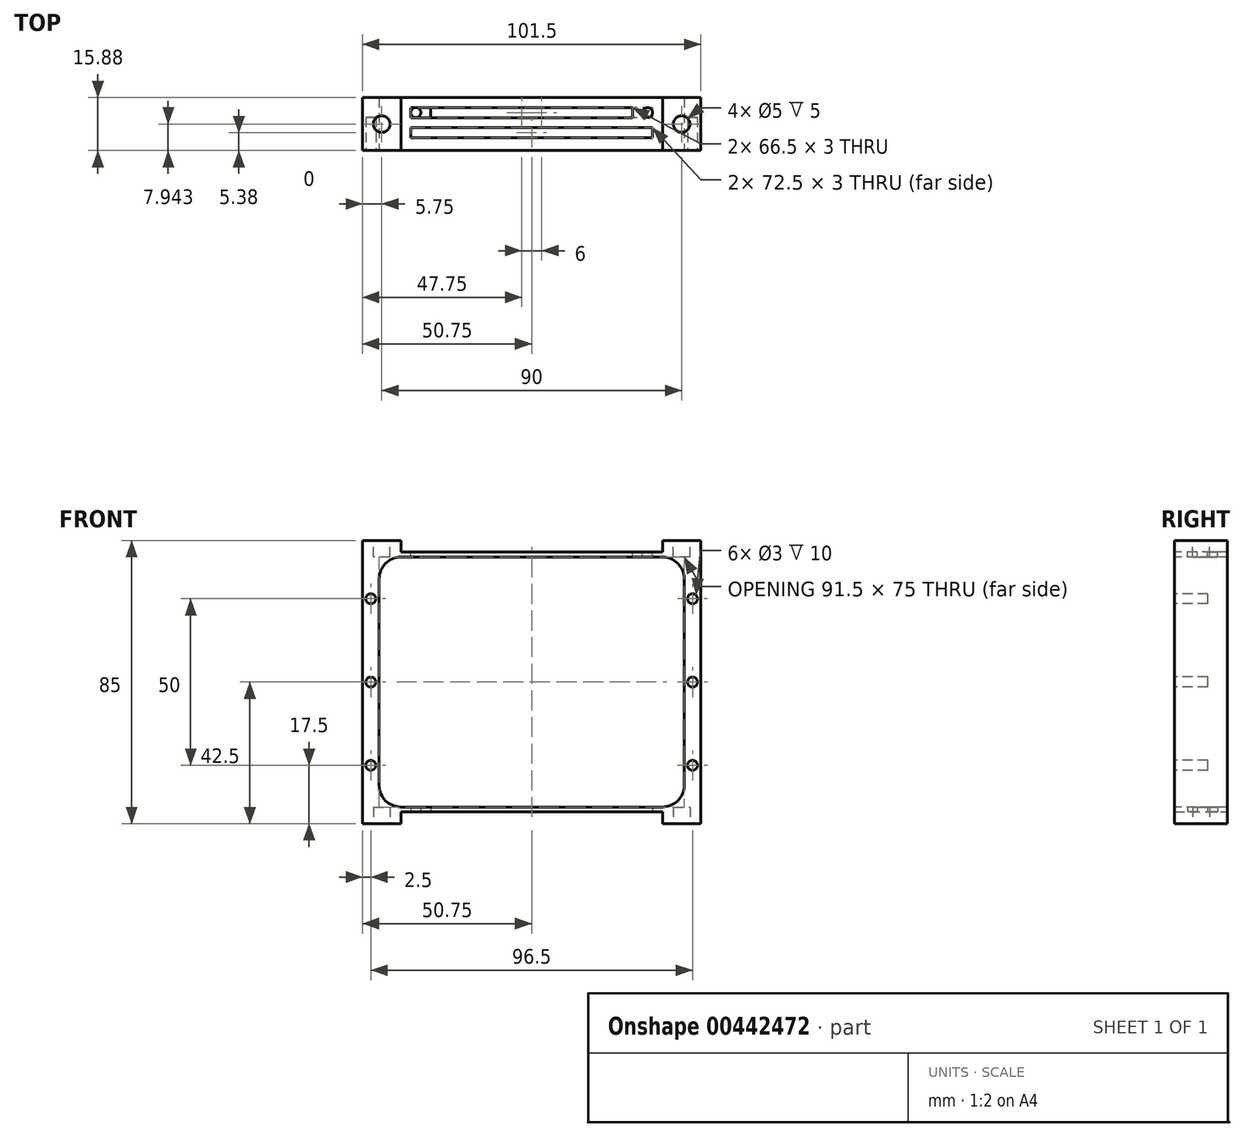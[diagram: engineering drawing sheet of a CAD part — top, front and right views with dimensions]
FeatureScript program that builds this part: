
annotation { "Feature Type Name" : "Feature", "Feature Type Description" : "" }
export const myFeature = defineFeature(function(context is Context, id is Id, definition is map)
    precondition{}
    {
        {
            var Q0;
            Q0=qCreatedBy(makeId("Front.planeOp"),FACE);
            var sketch = newSketch(context, id + "F0", { "sketchPlane" : qUnion([Q0])});
            skLineSegment(sketch, "E0.bottom", {"start": v(50.75, 42.5) * mm, "end": v(-50.75, 42.5) * mm});
            skLineSegment(sketch, "E0.top", {"start": v(50.75, -42.5) * mm, "end": v(-50.75, -42.5) * mm});
            skLineSegment(sketch, "E0.left", {"start": v(50.75, 42.5) * mm, "end": v(50.75, -42.5) * mm});
            skLineSegment(sketch, "E0.right", {"start": v(-50.75, 42.5) * mm, "end": v(-50.75, -42.5) * mm});
            skPoint(sketch, "E0.middle", {"position": v(0, 0) * mm});
            skSolve(sketch);
        }
        {
            var Q0;
            Q0=qSketchRegion(id+"F0",true);
            extrude(context, id + "F1", {"entities" : qUnion([Q0]), "depth" : 15.88 * mm});
        }
        {
            var Q0;
            Q0=makeQuery(id+"F1.opExtrude","CAP_FACE",FACE,{"disambiguationData":[OSD([sQuery(id+"F0.wireOp",EDGE,"E0.bottom"),sQuery(id+"F0.wireOp",EDGE,"E0.top"),sQuery(id+"F0.wireOp",EDGE,"E0.left"),sQuery(id+"F0.wireOp",EDGE,"E0.right")])],"isStart":false});
            var sketch = newSketch(context, id + "F2", { "sketchPlane" : qUnion([Q0])});
            skLineSegment(sketch, "E1.bottom", {"start": v(45.75, 37.5) * mm, "end": v(-45.75, 37.5) * mm, "construction": true});
            skLineSegment(sketch, "E1.top", {"start": v(45.75, -37.5) * mm, "end": v(-45.75, -37.5) * mm, "construction": true});
            skLineSegment(sketch, "E1.left", {"start": v(45.75, 37.5) * mm, "end": v(45.75, -37.5) * mm, "construction": true});
            skLineSegment(sketch, "E1.right", {"start": v(-45.75, 37.5) * mm, "end": v(-45.75, -37.5) * mm, "construction": true});
            skPoint(sketch, "E1.middle", {"position": v(0, 0) * mm});
            skCircle(sketch, "E2", {"center": v(-39.25, -31) * mm, "radius": 6.5 * mm, "construction": true});
            skCircle(sketch, "E3", {"center": v(39.25, -31) * mm, "radius": 6.5 * mm, "construction": true});
            skCircle(sketch, "E4", {"center": v(39.25, 31) * mm, "radius": 6.5 * mm, "construction": true});
            skLineSegment(sketch, "E5", {"start": v(-45.75, -31) * mm, "end": v(-45.75, 31) * mm});
            skLineSegment(sketch, "E6", {"start": v(-39.25, -37.5) * mm, "end": v(39.25, -37.5) * mm});
            skLineSegment(sketch, "E7", {"start": v(45.75, -31) * mm, "end": v(45.75, 31) * mm});
            skLineSegment(sketch, "E8", {"start": v(39.25, 37.5) * mm, "end": v(-39.25, 37.5) * mm});
            skArc(sketch, "E9", {"start": v(-39.25, 37.5) * mm, "mid": v(-43.85, 35.6) * mm, "end": v(-45.75, 31) * mm});
            skArc(sketch, "E10", {"start": v(-45.75, -31) * mm, "mid": v(-43.85, -35.6) * mm, "end": v(-39.25, -37.5) * mm});
            skArc(sketch, "E11", {"start": v(39.25, -37.5) * mm, "mid": v(43.85, -35.6) * mm, "end": v(45.75, -31) * mm});
            skArc(sketch, "E12", {"start": v(45.75, 31) * mm, "mid": v(43.85, 35.6) * mm, "end": v(39.25, 37.5) * mm});
            skSolve(sketch);
        }
        {
            var Q0;
            Q0=qSketchRegion(id+"F2",true);
            extrude(context, id + "F3", {"entities" : qUnion([Q0]), "operationType" : NewBodyOperationType.REMOVE, "oppositeDirection" : true, "depth" : 25 * mm});
        }
        {
            var Q0;
            Q0=makeQuery(id+"F1.opExtrude","SWEPT_FACE",FACE,{"disambiguationData":[OSD([sQuery(id+"F0.wireOp",EDGE,"E0.bottom")])]});
            var sketch = newSketch(context, id + "F4", { "sketchPlane" : qUnion([Q0])});
            skLineSegment(sketch, "E13.bottom", {"start": v(-39.25, 0) * mm, "end": v(39.25, 0) * mm});
            skLineSegment(sketch, "E13.top", {"start": v(-39.25, -15.88) * mm, "end": v(39.25, -15.88) * mm});
            skLineSegment(sketch, "E13.left", {"start": v(-39.25, 0) * mm, "end": v(-39.25, -15.88) * mm});
            skLineSegment(sketch, "E13.right", {"start": v(39.25, 0) * mm, "end": v(39.25, -15.88) * mm});
            skSolve(sketch);
        }
        {
            var Q0;
            Q0=qSketchRegion(id+"F4",true);
            extrude(context, id + "F5", {"entities" : qUnion([Q0]), "operationType" : NewBodyOperationType.REMOVE, "oppositeDirection" : true, "depth" : 3.5 * mm});
        }
        {
            var Q0;
            Q0=makeQuery(id+"F1.opExtrude","SWEPT_FACE",FACE,{"disambiguationData":[OSD([sQuery(id+"F0.wireOp",EDGE,"E0.top")])]});
            var sketch = newSketch(context, id + "F6", { "sketchPlane" : qUnion([Q0])});
            skLineSegment(sketch, "E14.bottom", {"start": v(-39.25, 15.88) * mm, "end": v(39.25, 15.88) * mm});
            skLineSegment(sketch, "E14.top", {"start": v(-39.25, 0) * mm, "end": v(39.25, 0) * mm});
            skLineSegment(sketch, "E14.left", {"start": v(-39.25, 15.88) * mm, "end": v(-39.25, 0) * mm});
            skLineSegment(sketch, "E14.right", {"start": v(39.25, 15.88) * mm, "end": v(39.25, 0) * mm});
            skSolve(sketch);
        }
        {
            var Q0;
            Q0=qSketchRegion(id+"F6",true);
            extrude(context, id + "F7", {"entities" : qUnion([Q0]), "operationType" : NewBodyOperationType.REMOVE, "oppositeDirection" : true, "depth" : 3.5 * mm});
        }
        {
            var Q0;
            Q0=makeQuery(id+"F5.boolean.opBoolean","COPY",FACE,{"derivedFrom":makeQuery(id+"F5.opExtrude","CAP_FACE",FACE,{"disambiguationData":[OSD([sQuery(id+"F4.wireOp",EDGE,"E13.bottom"),sQuery(id+"F4.wireOp",EDGE,"E13.top"),sQuery(id+"F4.wireOp",EDGE,"E13.left"),sQuery(id+"F4.wireOp",EDGE,"E13.right")])],"isStart":false})});
            var sketch = newSketch(context, id + "F8", { "sketchPlane" : qUnion([Q0])});
            skCircle(sketch, "E15", {"center": v(34.75, -4.5) * mm, "radius": 1.5 * mm});
            skLineSegment(sketch, "E16.bottom", {"start": v(-36.25, -3) * mm, "end": v(30.25, -3) * mm});
            skLineSegment(sketch, "E16.top", {"start": v(-36.25, -6) * mm, "end": v(30.25, -6) * mm});
            skLineSegment(sketch, "E16.left", {"start": v(-36.25, -3) * mm, "end": v(-36.25, -6) * mm});
            skLineSegment(sketch, "E16.right", {"start": v(30.25, -3) * mm, "end": v(30.25, -6) * mm});
            skLineSegment(sketch, "E17.bottom", {"start": v(-36.25, -9) * mm, "end": v(36.25, -9) * mm});
            skLineSegment(sketch, "E17.top", {"start": v(-36.25, -12) * mm, "end": v(36.25, -12) * mm});
            skLineSegment(sketch, "E17.left", {"start": v(-36.25, -9) * mm, "end": v(-36.25, -12) * mm});
            skLineSegment(sketch, "E17.right", {"start": v(36.25, -9) * mm, "end": v(36.25, -12) * mm});
            skSolve(sketch);
        }
        {
            var Q0;
            Q0=qSketchRegion(id+"F8",true);
            extrude(context, id + "F9", {"entities" : qUnion([Q0]), "operationType" : NewBodyOperationType.REMOVE, "oppositeDirection" : true, "depth" : 25 * mm});
        }
        {
            var Q0;
            Q0=makeQuery(id+"F7.boolean.opBoolean","COPY",FACE,{"derivedFrom":makeQuery(id+"F7.opExtrude","CAP_FACE",FACE,{"disambiguationData":[OSD([sQuery(id+"F6.wireOp",EDGE,"E14.bottom"),sQuery(id+"F6.wireOp",EDGE,"E14.top"),sQuery(id+"F6.wireOp",EDGE,"E14.left"),sQuery(id+"F6.wireOp",EDGE,"E14.right")])],"isStart":false})});
            var sketch = newSketch(context, id + "F10", { "sketchPlane" : qUnion([Q0])});
            skLineSegment(sketch, "E18.bottom", {"start": v(36.25, 9) * mm, "end": v(-36.25, 9) * mm});
            skLineSegment(sketch, "E18.top", {"start": v(36.25, 12) * mm, "end": v(-36.25, 12) * mm});
            skLineSegment(sketch, "E18.left", {"start": v(36.25, 9) * mm, "end": v(36.25, 12) * mm});
            skLineSegment(sketch, "E18.right", {"start": v(-36.25, 9) * mm, "end": v(-36.25, 12) * mm});
            skLineSegment(sketch, "E19.bottom", {"start": v(36.25, 3) * mm, "end": v(-30.25, 3) * mm});
            skLineSegment(sketch, "E19.top", {"start": v(36.25, 6) * mm, "end": v(-30.25, 6) * mm});
            skLineSegment(sketch, "E19.left", {"start": v(36.25, 3) * mm, "end": v(36.25, 6) * mm});
            skLineSegment(sketch, "E19.right", {"start": v(-30.25, 3) * mm, "end": v(-30.25, 6) * mm});
            skCircle(sketch, "E20", {"center": v(-34.75, 4.5) * mm, "radius": 1.5 * mm});
            skPoint(sketch, "E20.centerSnap0", {"position": v(-30.25, 4.5) * mm});
            skSolve(sketch);
        }
        {
            var Q0;
            Q0=qSketchRegion(id+"F10",true);
            extrude(context, id + "F11", {"entities" : qUnion([Q0]), "operationType" : NewBodyOperationType.REMOVE, "oppositeDirection" : true, "depth" : 25 * mm});
        }
        {
            var Q0;
            {var subQ0=sQuery(id+"F0.wireOp",EDGE,"E0.right");var subQ2=sQuery(id+"F0.wireOp",EDGE,"E0.top");Q0=makeQuery(id+"F7.boolean.opBoolean","SPLIT",FACE,{"disambiguationData":[TD([makeQuery(id+"F1.opExtrude","SWEPT_FACE",FACE,{"disambiguationData":[OSD([subQ0])]})])],"derivedFrom":makeQuery(id+"F1.opExtrude","SWEPT_FACE",FACE,{"disambiguationData":[OSD([subQ2])]})});}
            var sketch = newSketch(context, id + "F12", { "sketchPlane" : qUnion([Q0])});
            skLineSegment(sketch, "E21", {"start": v(-50.75, 15.87) * mm, "end": v(-39.25, 0) * mm, "construction": true});
            skCircle(sketch, "E22", {"center": v(-45, 7.94) * mm, "radius": 2.5 * mm});
            skPoint(sketch, "E22.centerSnap0", {"position": v(-50.75, 7.94) * mm});
            skSolve(sketch);
        }
        {
            var Q0;
            Q0=qSketchRegion(id+"F12",true);
            extrude(context, id + "F13", {"entities" : qUnion([Q0]), "operationType" : NewBodyOperationType.REMOVE, "oppositeDirection" : true, "depth" : 5 * mm});
        }
        {
            var Q0;
            {var subQ1=sQuery(id+"F0.wireOp",EDGE,"E0.left");var subQ2=sQuery(id+"F0.wireOp",EDGE,"E0.top");Q0=makeQuery(id+"F7.boolean.opBoolean","SPLIT",FACE,{"disambiguationData":[TD([makeQuery(id+"F1.opExtrude","SWEPT_FACE",FACE,{"disambiguationData":[OSD([subQ1])]})])],"derivedFrom":makeQuery(id+"F1.opExtrude","SWEPT_FACE",FACE,{"disambiguationData":[OSD([subQ2])]})});}
            var sketch = newSketch(context, id + "F14", { "sketchPlane" : qUnion([Q0])});
            skLineSegment(sketch, "E23", {"start": v(50.75, 15.88) * mm, "end": v(39.25, 0) * mm, "construction": true});
            skCircle(sketch, "E24", {"center": v(45, 7.94) * mm, "radius": 2.5 * mm});
            skSolve(sketch);
        }
        {
            var Q0;
            Q0=qSketchRegion(id+"F14",true);
            extrude(context, id + "F15", {"entities" : qUnion([Q0]), "operationType" : NewBodyOperationType.REMOVE, "oppositeDirection" : true, "depth" : 5 * mm});
        }
        {
            var Q0;
            {var subQ0=sQuery(id+"F0.wireOp",EDGE,"E0.right");var subQ3=sQuery(id+"F0.wireOp",EDGE,"E0.bottom");Q0=makeQuery(id+"F5.boolean.opBoolean","SPLIT",FACE,{"disambiguationData":[TD([makeQuery(id+"F1.opExtrude","SWEPT_FACE",FACE,{"disambiguationData":[OSD([subQ0])]})])],"derivedFrom":makeQuery(id+"F1.opExtrude","SWEPT_FACE",FACE,{"disambiguationData":[OSD([subQ3])]})});}
            var sketch = newSketch(context, id + "F16", { "sketchPlane" : qUnion([Q0])});
            skLineSegment(sketch, "E25", {"start": v(-50.75, 0) * mm, "end": v(-39.25, -15.88) * mm, "construction": true});
            skCircle(sketch, "E26", {"center": v(-45, -7.94) * mm, "radius": 2.5 * mm});
            skSolve(sketch);
        }
        {
            var Q0;
            Q0=qSketchRegion(id+"F16",true);
            extrude(context, id + "F17", {"entities" : qUnion([Q0]), "operationType" : NewBodyOperationType.REMOVE, "oppositeDirection" : true, "depth" : 5 * mm});
        }
        {
            var Q0;
            {var subQ1=sQuery(id+"F0.wireOp",EDGE,"E0.left");var subQ3=sQuery(id+"F0.wireOp",EDGE,"E0.bottom");Q0=makeQuery(id+"F5.boolean.opBoolean","SPLIT",FACE,{"disambiguationData":[TD([makeQuery(id+"F1.opExtrude","SWEPT_FACE",FACE,{"disambiguationData":[OSD([subQ1])]})])],"derivedFrom":makeQuery(id+"F1.opExtrude","SWEPT_FACE",FACE,{"disambiguationData":[OSD([subQ3])]})});}
            var sketch = newSketch(context, id + "F18", { "sketchPlane" : qUnion([Q0])});
            skLineSegment(sketch, "E27", {"start": v(50.75, 0) * mm, "end": v(39.25, -15.87) * mm, "construction": true});
            skCircle(sketch, "E28", {"center": v(45, -7.94) * mm, "radius": 2.5 * mm});
            skPoint(sketch, "E28.centerSnap0", {"position": v(45, -7.94) * mm});
            skSolve(sketch);
        }
        {
            var Q0;
            Q0=qSketchRegion(id+"F18",true);
            extrude(context, id + "F19", {"entities" : qUnion([Q0]), "operationType" : NewBodyOperationType.REMOVE, "oppositeDirection" : true, "depth" : 5 * mm});
        }
        {
            var Q0;
            Q0=makeQuery(id+"F1.opExtrude","CAP_FACE",FACE,{"disambiguationData":[OSD([sQuery(id+"F0.wireOp",EDGE,"E0.bottom"),sQuery(id+"F0.wireOp",EDGE,"E0.top"),sQuery(id+"F0.wireOp",EDGE,"E0.left"),sQuery(id+"F0.wireOp",EDGE,"E0.right")])],"isStart":false});
            var sketch = newSketch(context, id + "F20", { "sketchPlane" : qUnion([Q0])});
            skLineSegment(sketch, "E29", {"start": v(-48.25, 42.5) * mm, "end": v(-48.25, -42.5) * mm, "construction": true});
            skLineSegment(sketch, "E30", {"start": v(48.25, 42.5) * mm, "end": v(48.25, -42.5) * mm, "construction": true});
            skCircle(sketch, "E31", {"center": v(-48.25, 25) * mm, "radius": 1.5 * mm});
            skCircle(sketch, "E32", {"center": v(-48.25, 0) * mm, "radius": 1.5 * mm});
            skCircle(sketch, "E33", {"center": v(-48.25, -25) * mm, "radius": 1.5 * mm});
            skCircle(sketch, "E34", {"center": v(48.25, -25) * mm, "radius": 1.5 * mm});
            skCircle(sketch, "E35", {"center": v(48.25, 0) * mm, "radius": 1.5 * mm});
            skCircle(sketch, "E36", {"center": v(48.25, 25) * mm, "radius": 1.5 * mm});
            skSolve(sketch);
        }
        {
            var Q0;
            Q0=qSketchRegion(id+"F20",true);
            extrude(context, id + "F21", {"entities" : qUnion([Q0]), "operationType" : NewBodyOperationType.REMOVE, "oppositeDirection" : true, "depth" : 10 * mm});
        }
    });
